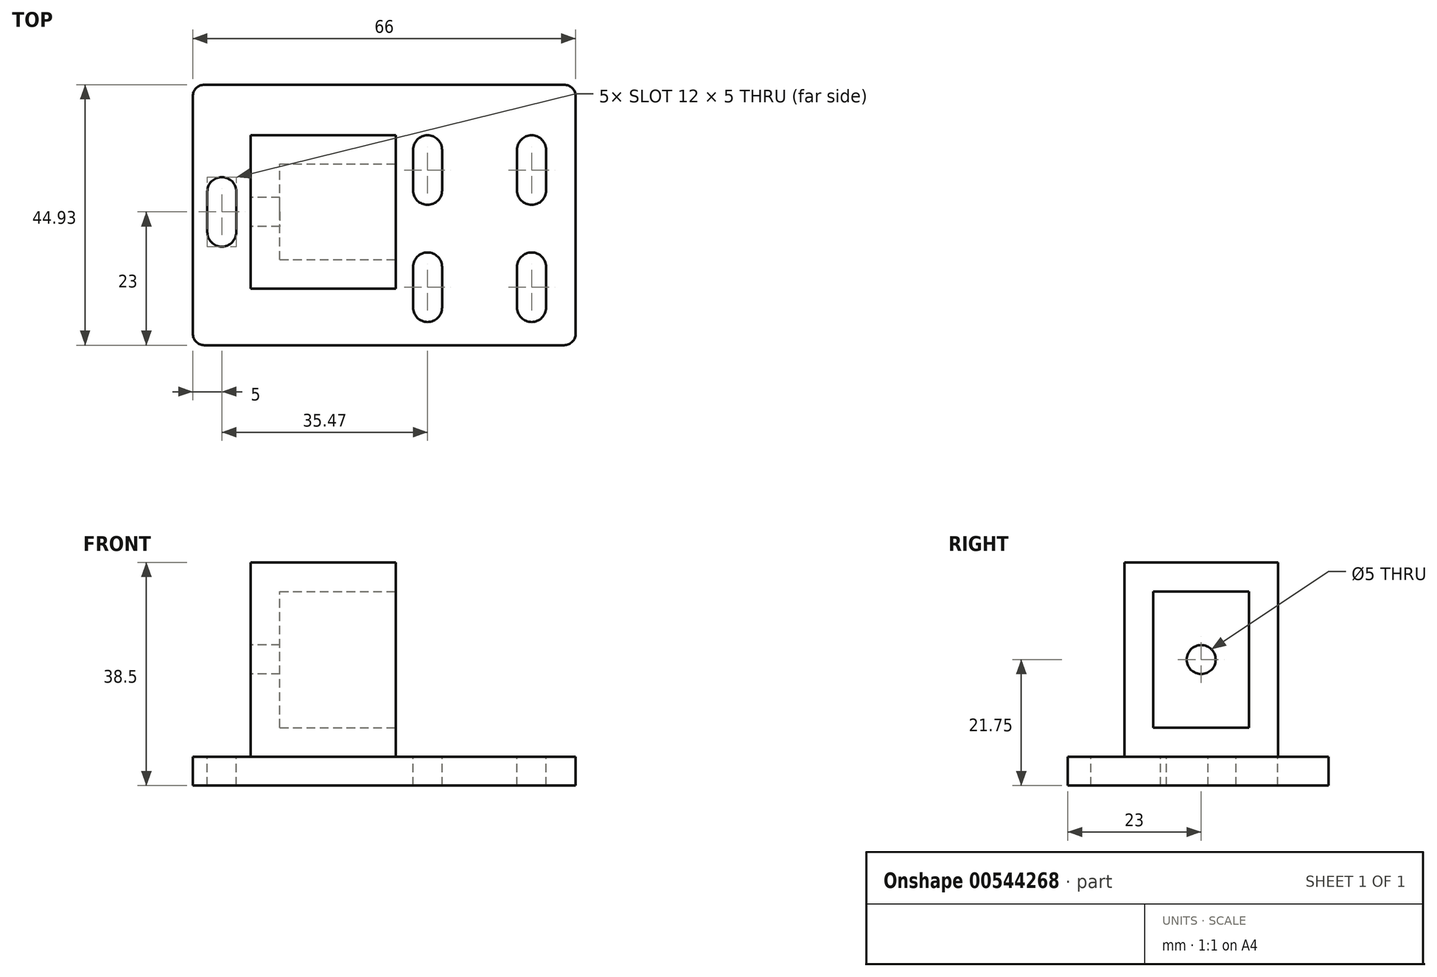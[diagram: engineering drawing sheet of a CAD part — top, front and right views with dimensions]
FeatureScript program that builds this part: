
annotation { "Feature Type Name" : "Feature", "Feature Type Description" : "" }
export const myFeature = defineFeature(function(context is Context, id is Id, definition is map)
    precondition{}
    {
        {
            var Q0;
            Q0=qCreatedBy(makeId("Right.planeOp"),FACE);
            var sketch = newSketch(context, id + "F0", { "sketchPlane" : qUnion([Q0])});
            skLineSegment(sketch, "E0.bottom", {"start": v(-5, -5) * mm, "end": v(-5, 28.5) * mm});
            skLineSegment(sketch, "E0.top", {"start": v(21.5, -5) * mm, "end": v(21.5, 28.5) * mm});
            skLineSegment(sketch, "E0.left", {"start": v(-5, -5) * mm, "end": v(21.5, -5) * mm});
            skLineSegment(sketch, "E0.right", {"start": v(-5, 28.5) * mm, "end": v(21.5, 28.5) * mm});
            skSolve(sketch);
        }
        {
            var Q0;
            Q0=makeQuery(id+"F0.imprint","IMPRINT",FACE,{"disambiguationData":[TD([[makeQuery(id+"F0.imprint","IMPRINT",EDGE,{"derivedFrom":sQuery(id+"F0.wireOp",EDGE,"E0.bottom")}),-1.0]])]});
            var Q1;
            {var subQ0=sQuery(id+"F0.wireOp",EDGE,"ZHw5m0qF-6T86-iuNP-7Xns-RyXjLZ7WSVfi");Q1=makeQuery(id+"F0.imprint","IMPRINT",FACE,{"disambiguationData":[TD([[makeQuery(id+"F0.imprint","IMPRINT",EDGE,{"derivedFrom":subQ0}),1.0]])]});}
            extrude(context, id + "F1", {"entities" : qUnion([Q0, Q1]), "depth" : 25 * mm, "offsetDistance" : 25 * mm});
        }
        {
            var Q0;
            Q0=makeQuery(id+"F1.opExtrude","CAP_FACE",FACE,{"disambiguationData":[OSD([sQuery(id+"F0.wireOp",EDGE,"E0.bottom"),sQuery(id+"F0.wireOp",EDGE,"E0.top"),sQuery(id+"F0.wireOp",EDGE,"E0.left"),sQuery(id+"F0.wireOp",EDGE,"E0.right"),sQuery(id+"F0.wireOp",EDGE,"ZHw5m0qF-6T86-iuNP-7Xns-RyXjLZ7WSVfi"),sQuery(id+"F0.wireOp",EDGE,"VlUIqmLF-rVp9-osWc-qdkI-81NK7IL85w5T"),sQuery(id+"F0.wireOp",EDGE,"hCYKgD8Z-p7oS-FlZl-bt9Q-rGw9J13IuOz8.bottom")])],"isStart":false});
            var sketch = newSketch(context, id + "F2", { "sketchPlane" : qUnion([Q0])});
            skLineSegment(sketch, "E1.bottom", {"start": v(0, 0) * mm, "end": v(0, 23.5) * mm});
            skLineSegment(sketch, "E1.top", {"start": v(16.5, 0) * mm, "end": v(16.5, 23.5) * mm});
            skLineSegment(sketch, "E1.left", {"start": v(0, 0) * mm, "end": v(16.5, 0) * mm});
            skLineSegment(sketch, "E1.right", {"start": v(0, 23.5) * mm, "end": v(16.5, 23.5) * mm});
            skSolve(sketch);
        }
        {
            var Q0;
            Q0=makeQuery(id+"F2.imprint","IMPRINT",FACE,{"disambiguationData":[TD([[makeQuery(id+"F2.imprint","IMPRINT",EDGE,{"derivedFrom":sQuery(id+"F2.wireOp",EDGE,"E1.bottom")}),-1.0]])]});
            extrude(context, id + "F3", {"entities" : qUnion([Q0]), "operationType" : NewBodyOperationType.REMOVE, "oppositeDirection" : true, "depth" : 20 * mm, "offsetDistance" : 25 * mm});
        }
        {
            var Q0;
            Q0=makeQuery(id+"F1.opExtrude","CAP_FACE",FACE,{"disambiguationData":[OSD([sQuery(id+"F0.wireOp",EDGE,"E0.bottom"),sQuery(id+"F0.wireOp",EDGE,"E0.top"),sQuery(id+"F0.wireOp",EDGE,"E0.left"),sQuery(id+"F0.wireOp",EDGE,"E0.right"),sQuery(id+"F0.wireOp",EDGE,"ZHw5m0qF-6T86-iuNP-7Xns-RyXjLZ7WSVfi"),sQuery(id+"F0.wireOp",EDGE,"VlUIqmLF-rVp9-osWc-qdkI-81NK7IL85w5T"),sQuery(id+"F0.wireOp",EDGE,"hCYKgD8Z-p7oS-FlZl-bt9Q-rGw9J13IuOz8.bottom")])],"isStart":true});
            var sketch = newSketch(context, id + "F4", { "sketchPlane" : qUnion([Q0])});
            skCircle(sketch, "E2", {"center": v(-8.25, 11.75) * mm, "radius": 2.5 * mm});
            skSolve(sketch);
        }
        {
            var Q0;
            Q0=makeQuery(id+"F4.imprint","IMPRINT",FACE,{"disambiguationData":[TD([[makeQuery(id+"F4.imprint","IMPRINT",EDGE,{"derivedFrom":sQuery(id+"F4.wireOp",EDGE,"E2")}),1.0]])]});
            extrude(context, id + "F5", {"entities" : qUnion([Q0]), "operationType" : NewBodyOperationType.REMOVE, "endBound" : BoundingType.THROUGH_ALL, "oppositeDirection" : true, "depth" : 25 * mm, "offsetDistance" : 25 * mm});
        }
        {
            var Q0;
            Q0=makeQuery(id+"F1.opExtrude","CAP_FACE",FACE,{"disambiguationData":[OSD([sQuery(id+"F0.wireOp",EDGE,"E0.bottom"),sQuery(id+"F0.wireOp",EDGE,"E0.top"),sQuery(id+"F0.wireOp",EDGE,"E0.left"),sQuery(id+"F0.wireOp",EDGE,"E0.right"),sQuery(id+"F0.wireOp",EDGE,"ZHw5m0qF-6T86-iuNP-7Xns-RyXjLZ7WSVfi"),sQuery(id+"F0.wireOp",EDGE,"VlUIqmLF-rVp9-osWc-qdkI-81NK7IL85w5T"),sQuery(id+"F0.wireOp",EDGE,"hCYKgD8Z-p7oS-FlZl-bt9Q-rGw9J13IuOz8.bottom")])],"isStart":false});
            var sketch = newSketch(context, id + "F6", { "sketchPlane" : qUnion([Q0])});
            skLineSegment(sketch, "E3.bottom", {"start": v(-14.75, -5) * mm, "end": v(30.18, -5) * mm});
            skLineSegment(sketch, "E3.top", {"start": v(-14.75, -10) * mm, "end": v(30.18, -10) * mm});
            skLineSegment(sketch, "E3.left", {"start": v(-14.75, -5) * mm, "end": v(-14.75, -10) * mm});
            skLineSegment(sketch, "E3.right", {"start": v(30.18, -5) * mm, "end": v(30.18, -10) * mm});
            skSolve(sketch);
        }
        {
            var Q0;
            Q0=makeQuery(id+"F6.imprint","IMPRINT",FACE,{"disambiguationData":[TD([[makeQuery(id+"F6.imprint","IMPRINT",EDGE,{"derivedFrom":sQuery(id+"F6.wireOp",EDGE,"E3.top")}),1.0]])]});
            extrude(context, id + "F7", {"entities" : qUnion([Q0]), "operationType" : NewBodyOperationType.ADD, "depth" : 31 * mm, "offsetDistance" : 25 * mm, "hasSecondDirection" : true, "secondDirectionOppositeDirection" : true, "secondDirectionDepth" : 35 * mm});
        }
        {
            var Q0;
            Q0=makeQuery(id+"F7.opExtrude","CAP_EDGE",EDGE,{"disambiguationData":[OSD([sQuery(id+"F6.wireOp",EDGE,"E3.left")])],"isStart":false});
            var Q1;
            Q1=makeQuery(id+"F7.opExtrude","CAP_EDGE",EDGE,{"disambiguationData":[OSD([sQuery(id+"F6.wireOp",EDGE,"E3.right")])],"isStart":false});
            var Q2;
            Q2=makeQuery(id+"F7.opExtrude","CAP_EDGE",EDGE,{"disambiguationData":[OSD([sQuery(id+"F6.wireOp",EDGE,"E3.left")])],"isStart":true});
            var Q3;
            Q3=makeQuery(id+"F7.opExtrude","CAP_EDGE",EDGE,{"disambiguationData":[OSD([sQuery(id+"F6.wireOp",EDGE,"E3.right")])],"isStart":true});
            fillet(context, id + "F8", {"entities" : qUnion([Q0, Q1, Q2, Q3]), "radius" : 2 * mm, "tangentPropagation" : true, "allowEdgeOverflow" : false});
        }
        {
            var Q0;
            Q0=makeQuery(id+"F7.opExtrude","SWEPT_FACE",FACE,{"disambiguationData":[OSD([sQuery(id+"F6.wireOp",EDGE,"E3.bottom")])]});
            var sketch = newSketch(context, id + "F9", { "sketchPlane" : qUnion([Q0])});
            skLineSegment(sketch, "E4.bottom", {"start": v(30.47, 21.46) * mm, "end": v(30.47, 21.46) * mm});
            skLineSegment(sketch, "E4.top", {"start": v(30.47, 9.46) * mm, "end": v(30.47, 9.46) * mm});
            skLineSegment(sketch, "E4.left", {"start": v(27.97, 18.96) * mm, "end": v(27.97, 11.96) * mm});
            skLineSegment(sketch, "E4.right", {"start": v(32.97, 18.96) * mm, "end": v(32.97, 11.96) * mm});
            skLineSegment(sketch, "E5.bottom", {"start": v(30.47, 1.25) * mm, "end": v(30.47, 1.25) * mm});
            skLineSegment(sketch, "E5.top", {"start": v(30.47, -10.75) * mm, "end": v(30.47, -10.75) * mm});
            skLineSegment(sketch, "E5.left", {"start": v(27.97, -1.25) * mm, "end": v(27.97, -8.25) * mm});
            skLineSegment(sketch, "E5.right", {"start": v(32.97, -1.25) * mm, "end": v(32.97, -8.25) * mm});
            skPoint(sketch, "E6.visualSharp", {"position": v(27.97, 21.46) * mm});
            skArc(sketch, "E6.filletArc", {"start": v(30.47, 21.46) * mm, "mid": v(28.7, 20.73) * mm, "end": v(27.97, 18.96) * mm});
            skPoint(sketch, "E7.visualSharp", {"position": v(32.97, 21.46) * mm});
            skArc(sketch, "E7.filletArc", {"start": v(32.97, 18.96) * mm, "mid": v(32.24, 20.73) * mm, "end": v(30.47, 21.46) * mm});
            skPoint(sketch, "E8.visualSharp", {"position": v(32.97, 9.46) * mm});
            skArc(sketch, "E8.filletArc", {"start": v(30.47, 9.46) * mm, "mid": v(32.24, 10.2) * mm, "end": v(32.97, 11.96) * mm});
            skPoint(sketch, "E9.visualSharp", {"position": v(27.97, 9.46) * mm});
            skArc(sketch, "E9.filletArc", {"start": v(27.97, 11.96) * mm, "mid": v(28.7, 10.2) * mm, "end": v(30.47, 9.46) * mm});
            skPoint(sketch, "E10.visualSharp", {"position": v(32.97, 1.25) * mm});
            skArc(sketch, "E10.filletArc", {"start": v(32.97, -1.25) * mm, "mid": v(32.24, 0.52) * mm, "end": v(30.47, 1.25) * mm});
            skPoint(sketch, "E11.visualSharp", {"position": v(27.97, 1.25) * mm});
            skArc(sketch, "E11.filletArc", {"start": v(30.47, 1.25) * mm, "mid": v(28.7, 0.52) * mm, "end": v(27.97, -1.25) * mm});
            skPoint(sketch, "E12.visualSharp", {"position": v(32.97, -10.75) * mm});
            skArc(sketch, "E12.filletArc", {"start": v(30.47, -10.75) * mm, "mid": v(32.24, -10.02) * mm, "end": v(32.97, -8.25) * mm});
            skPoint(sketch, "E13.visualSharp", {"position": v(27.97, -10.75) * mm});
            skArc(sketch, "E13.filletArc", {"start": v(27.97, -8.25) * mm, "mid": v(28.7, -10.02) * mm, "end": v(30.47, -10.75) * mm});
            skLineSegment(sketch, "E14.bottom", {"start": v(48.4, 21.46) * mm, "end": v(48.4, 21.46) * mm});
            skLineSegment(sketch, "E14.top", {"start": v(48.4, 9.46) * mm, "end": v(48.4, 9.46) * mm});
            skLineSegment(sketch, "E14.left", {"start": v(45.9, 18.96) * mm, "end": v(45.9, 11.96) * mm});
            skLineSegment(sketch, "E14.right", {"start": v(50.9, 18.96) * mm, "end": v(50.9, 11.96) * mm});
            skPoint(sketch, "E15.visualSharp", {"position": v(45.9, 21.46) * mm});
            skArc(sketch, "E15.filletArc", {"start": v(48.4, 21.46) * mm, "mid": v(46.63, 20.73) * mm, "end": v(45.9, 18.96) * mm});
            skPoint(sketch, "E16.visualSharp", {"position": v(50.9, 21.46) * mm});
            skArc(sketch, "E16.filletArc", {"start": v(50.9, 18.96) * mm, "mid": v(50.17, 20.73) * mm, "end": v(48.4, 21.46) * mm});
            skPoint(sketch, "E17.visualSharp", {"position": v(45.9, 9.46) * mm});
            skArc(sketch, "E17.filletArc", {"start": v(45.9, 11.96) * mm, "mid": v(46.63, 10.2) * mm, "end": v(48.4, 9.46) * mm});
            skPoint(sketch, "E18.visualSharp", {"position": v(50.9, 9.46) * mm});
            skArc(sketch, "E18.filletArc", {"start": v(48.4, 9.46) * mm, "mid": v(50.17, 10.2) * mm, "end": v(50.9, 11.96) * mm});
            skLineSegment(sketch, "E19.bottom", {"start": v(48.4, 1.25) * mm, "end": v(48.4, 1.25) * mm});
            skLineSegment(sketch, "E19.top", {"start": v(48.4, -10.75) * mm, "end": v(48.4, -10.75) * mm});
            skLineSegment(sketch, "E19.left", {"start": v(45.9, -1.25) * mm, "end": v(45.9, -8.25) * mm});
            skLineSegment(sketch, "E19.right", {"start": v(50.9, -1.25) * mm, "end": v(50.9, -8.25) * mm});
            skPoint(sketch, "E20.visualSharp", {"position": v(45.9, 1.25) * mm});
            skArc(sketch, "E20.filletArc", {"start": v(48.4, 1.25) * mm, "mid": v(46.63, 0.52) * mm, "end": v(45.9, -1.25) * mm});
            skPoint(sketch, "E21.visualSharp", {"position": v(50.9, 1.25) * mm});
            skArc(sketch, "E21.filletArc", {"start": v(50.9, -1.25) * mm, "mid": v(50.17, 0.52) * mm, "end": v(48.4, 1.25) * mm});
            skPoint(sketch, "E22.visualSharp", {"position": v(45.9, -10.75) * mm});
            skArc(sketch, "E22.filletArc", {"start": v(45.9, -8.25) * mm, "mid": v(46.63, -10.02) * mm, "end": v(48.4, -10.75) * mm});
            skPoint(sketch, "E23.visualSharp", {"position": v(50.9, -10.75) * mm});
            skArc(sketch, "E23.filletArc", {"start": v(48.4, -10.75) * mm, "mid": v(50.17, -10.02) * mm, "end": v(50.9, -8.25) * mm});
            skLineSegment(sketch, "E24.bottom", {"start": v(-5, 14.25) * mm, "end": v(-5, 14.25) * mm});
            skLineSegment(sketch, "E24.top", {"start": v(-5, 2.25) * mm, "end": v(-5, 2.25) * mm});
            skLineSegment(sketch, "E24.left", {"start": v(-7.5, 11.75) * mm, "end": v(-7.5, 4.75) * mm});
            skLineSegment(sketch, "E24.right", {"start": v(-2.5, 11.75) * mm, "end": v(-2.5, 4.75) * mm});
            skPoint(sketch, "E25.visualSharp", {"position": v(-7.5, 14.25) * mm});
            skArc(sketch, "E25.filletArc", {"start": v(-5, 14.25) * mm, "mid": v(-6.77, 13.52) * mm, "end": v(-7.5, 11.75) * mm});
            skPoint(sketch, "E26.visualSharp", {"position": v(-2.5, 14.25) * mm});
            skArc(sketch, "E26.filletArc", {"start": v(-2.5, 11.75) * mm, "mid": v(-3.23, 13.52) * mm, "end": v(-5, 14.25) * mm});
            skPoint(sketch, "E27.visualSharp", {"position": v(-7.5, 2.25) * mm});
            skArc(sketch, "E27.filletArc", {"start": v(-7.5, 4.75) * mm, "mid": v(-6.77, 2.98) * mm, "end": v(-5, 2.25) * mm});
            skPoint(sketch, "E28.visualSharp", {"position": v(-2.5, 2.25) * mm});
            skArc(sketch, "E28.filletArc", {"start": v(-5, 2.25) * mm, "mid": v(-3.23, 2.98) * mm, "end": v(-2.5, 4.75) * mm});
            skSolve(sketch);
        }
        {
            var Q0;
            Q0 = qSketchRegion(id + "F9", true);
            extrude(context, id + "F10", {"entities" : qUnion([Q0]), "operationType" : NewBodyOperationType.REMOVE, "endBound" : BoundingType.UP_TO_NEXT, "oppositeDirection" : true, "depth" : 25 * mm, "offsetDistance" : 25 * mm});
        }
    });
